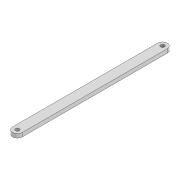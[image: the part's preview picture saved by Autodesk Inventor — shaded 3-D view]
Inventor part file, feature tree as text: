
AUTODESK INVENTOR PART (.ipt)
format: ipt  version: 2022 (Build 260153000, 153)  size: 82,944 bytes
history: native  units: mm
features: extrude x1, sketch x1
ambient origin geometry x8: Origin, YZ Plane, XZ Plane, XY Plane, X Axis, Y Axis, Z Axis, Center Point
bodies: Solid1 (feature_tree)
feature tree (2):
  extrude  "Extrusion1"  Depth=10.0mm
  sketch  "Sketch1"  dims[d0=150.0mm d1=10.0mm d2=4.0mm d3=4.0mm d4=4.0mm d5=0.0mm]
